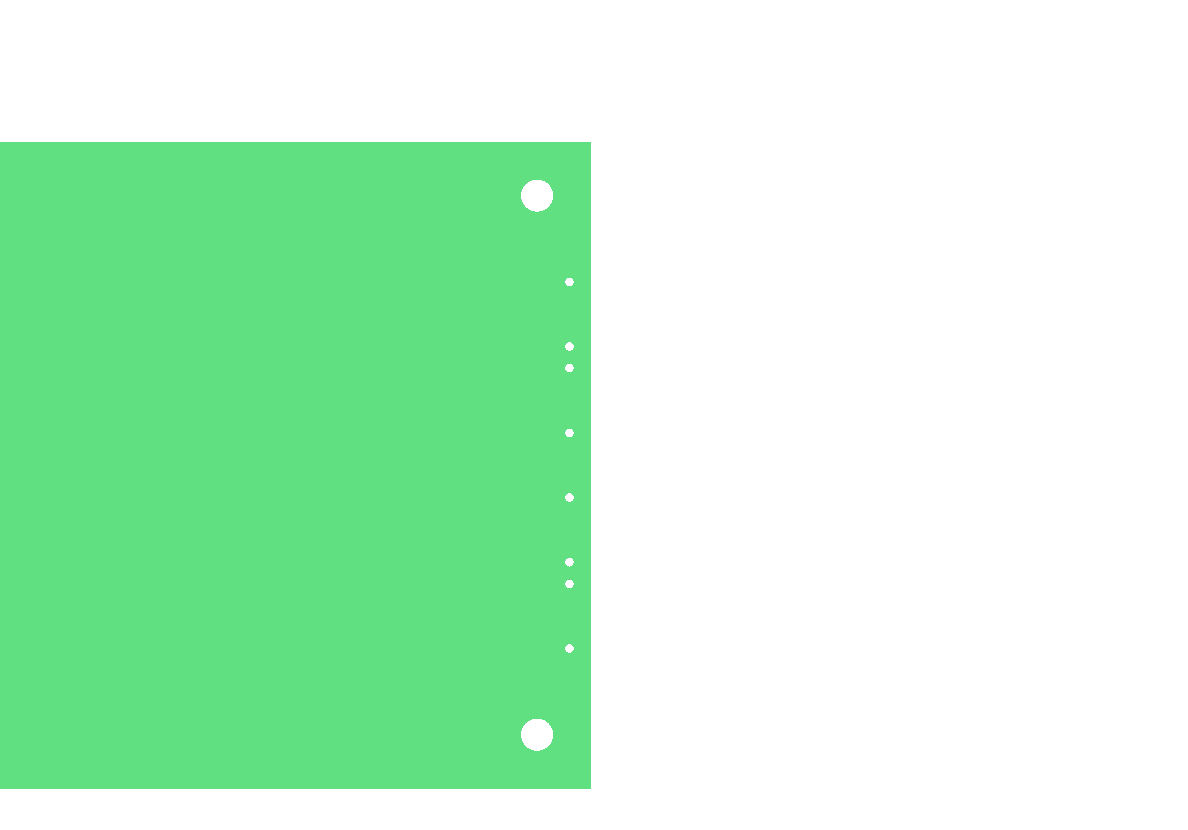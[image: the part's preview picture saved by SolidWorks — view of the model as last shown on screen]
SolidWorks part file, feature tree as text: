
SOLIDWORKS PART (.sldprt)
format: sldprt  version: not decoded by parser v0  size: 333,824 bytes
history: native  units: mm
features: sketch x4, cut_extrude x3, material x1, extrude x1, pattern_linear x1 (+13 scaffold rows collapsed)
feature tree (23):
  scaffold x13  (default folders/planes/origin — collapsed)
  material  "Material <not specified>"
  sketch  "Sketch1"  dims[D1=158.75mm D2=76.2mm]
  extrude  "Extrude1"  Depth=1.5748mm
  sketch  "Sketch2"  dims[c1.D1=~1.999298mm c1.D5=3.81mm c1.D6=3.81mm c1.D11=3.81mm c1.D12=3.81mm c2.D1=6.35mm c2.D2=6.35mm c2.D3=6.35mm c2.D4=6.35mm c2.D7=6.35mm c2.D8=6.35mm c2.D9=6.35mm c2.D10=6.35mm]
  cut_extrude  "Cut-Extrude2"  Depth=1.5748mm
  sketch  "Sketch4"  dims[c1.D1=1.3mm c1.D2=1.3mm c1.D10=1.0mm c1.D11=1.0mm c1.D3=~19.234912mm c1.D4=7.55mm c1.D5=~19.234912mm c1.D6=7.55mm c1.D7=~37.730176mm c1.D8=43.53mm c1.D9=5.95mm c1.D12=~36.528293mm c1.D13=~39.671707mm c2.D12=~16.334994mm c2.D13=~16.335006mm]
  cut_extrude  "Cut-Extrude3"  Depth=1.5748mm
  sketch  "Sketch5"  dims[D1=1.016mm D7=1.016mm D8=1.016mm D9=1.016mm D2=16.51mm D3=2.54mm D4=7.62mm D5=2.54mm D6=7.62mm]
  cut_extrude  "transceiver holes"  Depth=2.54mm
  pattern_linear  "LPattern1"  Count1=2 Count2=1 Spacing1=25.4mm Spacing2=7.62mm
decode coverage: 9 of 9 modeling features carry decoded parameters
note: ~ marks probable driven/reference dimensions
note: suppression state not decoded; provenance and decode notes live in map.json
